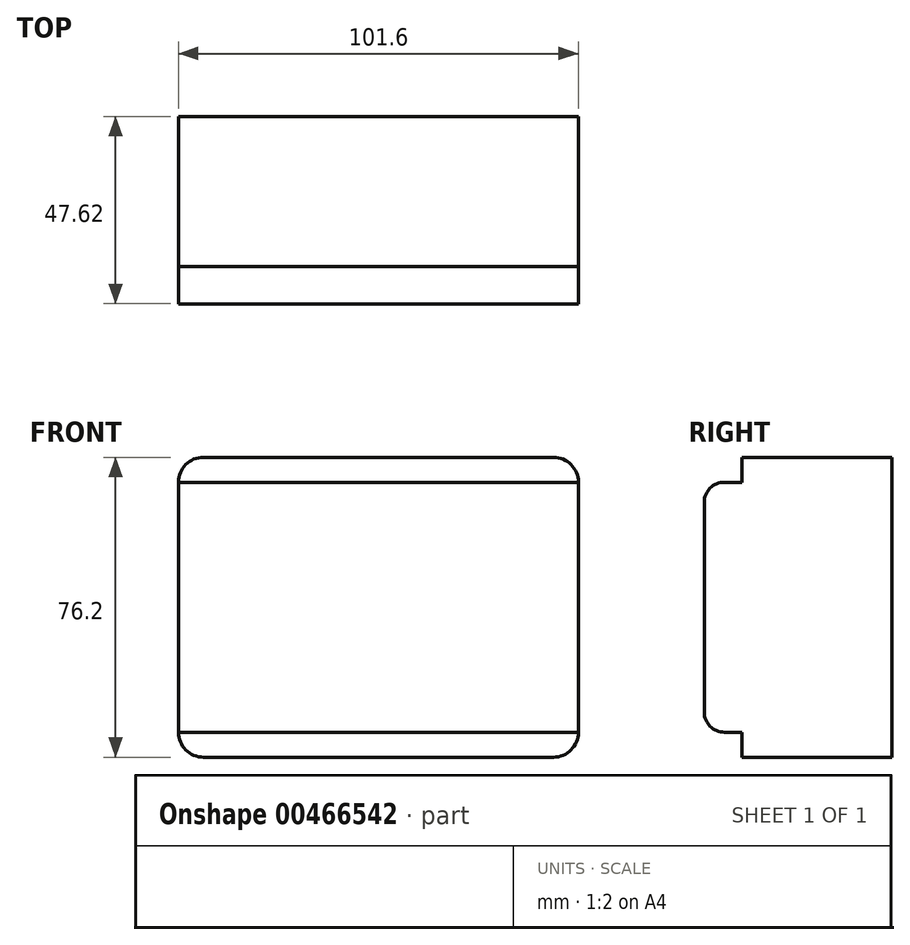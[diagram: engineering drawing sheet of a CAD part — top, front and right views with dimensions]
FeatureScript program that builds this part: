
annotation { "Feature Type Name" : "Feature", "Feature Type Description" : "" }
export const myFeature = defineFeature(function(context is Context, id is Id, definition is map)
    precondition{}
    {
        {
            var Q0;
            Q0=qCreatedBy(makeId("Front.planeOp"),FACE);
            var sketch = newSketch(context, id + "F0", { "sketchPlane" : qUnion([Q0])});
            skLineSegment(sketch, "E0.bottom", {"start": v(50.8, -38.1) * mm, "end": v(-50.8, -38.1) * mm});
            skLineSegment(sketch, "E0.top", {"start": v(50.8, 38.1) * mm, "end": v(-50.8, 38.1) * mm});
            skLineSegment(sketch, "E0.left", {"start": v(50.8, -38.1) * mm, "end": v(50.8, 38.1) * mm});
            skLineSegment(sketch, "E0.right", {"start": v(-50.8, -38.1) * mm, "end": v(-50.8, 38.1) * mm});
            skPoint(sketch, "E0.middle", {"position": v(0, 0) * mm});
            skSolve(sketch);
        }
        {
            var Q0;
            Q0=makeQuery(id+"F0.imprint","IMPRINT",FACE,{"disambiguationData":[TD([[makeQuery(id+"F0.imprint","IMPRINT",EDGE,{"derivedFrom":sQuery(id+"F0.wireOp",EDGE,"E0.bottom")}),-1.0]])]});
            extrude(context, id + "F1", {"entities" : qUnion([Q0]), "depth" : 38.1 * mm});
        }
        {
            var Q0;
            Q0=makeQuery(id+"F1.opExtrude","SWEPT_EDGE",EDGE,{"disambiguationData":[OSD([sQuery(id+"F0.wireOp",EDGE,"E0.bottom"),sQuery(id+"F0.wireOp",EDGE,"E0.left")])]});
            var Q1;
            Q1=makeQuery(id+"F1.opExtrude","SWEPT_EDGE",EDGE,{"disambiguationData":[OSD([sQuery(id+"F0.wireOp",EDGE,"E0.top"),sQuery(id+"F0.wireOp",EDGE,"E0.left")])]});
            var Q2;
            Q2=makeQuery(id+"F1.opExtrude","SWEPT_EDGE",EDGE,{"disambiguationData":[OSD([sQuery(id+"F0.wireOp",EDGE,"E0.top"),sQuery(id+"F0.wireOp",EDGE,"E0.right")])]});
            var Q3;
            Q3=makeQuery(id+"F1.opExtrude","SWEPT_EDGE",EDGE,{"disambiguationData":[OSD([sQuery(id+"F0.wireOp",EDGE,"E0.bottom"),sQuery(id+"F0.wireOp",EDGE,"E0.right")])]});
            fillet(context, id + "F2", {"entities" : qUnion([Q0, Q1, Q2, Q3]), "radius" : 6.35 * mm, "tangentPropagation" : true, "allowEdgeOverflow" : false});
        }
        {
            var Q0;
            Q0=makeQuery(id+"F1.opExtrude","CAP_FACE",FACE,{"disambiguationData":[OSD([sQuery(id+"F0.wireOp",EDGE,"E0.bottom"),sQuery(id+"F0.wireOp",EDGE,"E0.top"),sQuery(id+"F0.wireOp",EDGE,"E0.left"),sQuery(id+"F0.wireOp",EDGE,"E0.right")])],"isStart":false});
            var sketch = newSketch(context, id + "F3", { "sketchPlane" : qUnion([Q0])});
            skLineSegment(sketch, "E1.bottom", {"start": v(50.8, -31.75) * mm, "end": v(-50.8, -31.75) * mm});
            skLineSegment(sketch, "E1.top", {"start": v(50.8, 31.75) * mm, "end": v(-50.8, 31.75) * mm});
            skLineSegment(sketch, "E1.left", {"start": v(50.8, -31.75) * mm, "end": v(50.8, 31.75) * mm});
            skLineSegment(sketch, "E1.right", {"start": v(-50.8, -31.75) * mm, "end": v(-50.8, 31.75) * mm});
            skPoint(sketch, "E1.middle", {"position": v(0, 0) * mm});
            skSolve(sketch);
        }
        {
            var Q0;
            Q0=makeQuery(id+"F3.imprint","IMPRINT",FACE,{"disambiguationData":[TD([[makeQuery(id+"F3.imprint","IMPRINT",EDGE,{"derivedFrom":sQuery(id+"F3.wireOp",EDGE,"E1.bottom")}),-1.0]])]});
            extrude(context, id + "F4", {"entities" : qUnion([Q0]), "operationType" : NewBodyOperationType.ADD, "depth" : 9.52 * mm});
        }
        {
            var Q0;
            Q0=makeQuery(id+"F4.opExtrude","CAP_EDGE",EDGE,{"disambiguationData":[OSD([sQuery(id+"F3.wireOp",EDGE,"E1.top")])],"isStart":false});
            var Q1;
            Q1=makeQuery(id+"F4.opExtrude","CAP_EDGE",EDGE,{"disambiguationData":[OSD([sQuery(id+"F3.wireOp",EDGE,"E1.bottom")])],"isStart":false});
            fillet(context, id + "F5", {"entities" : qUnion([Q0, Q1]), "radius" : 5.08 * mm, "tangentPropagation" : true, "allowEdgeOverflow" : false});
        }
    });
